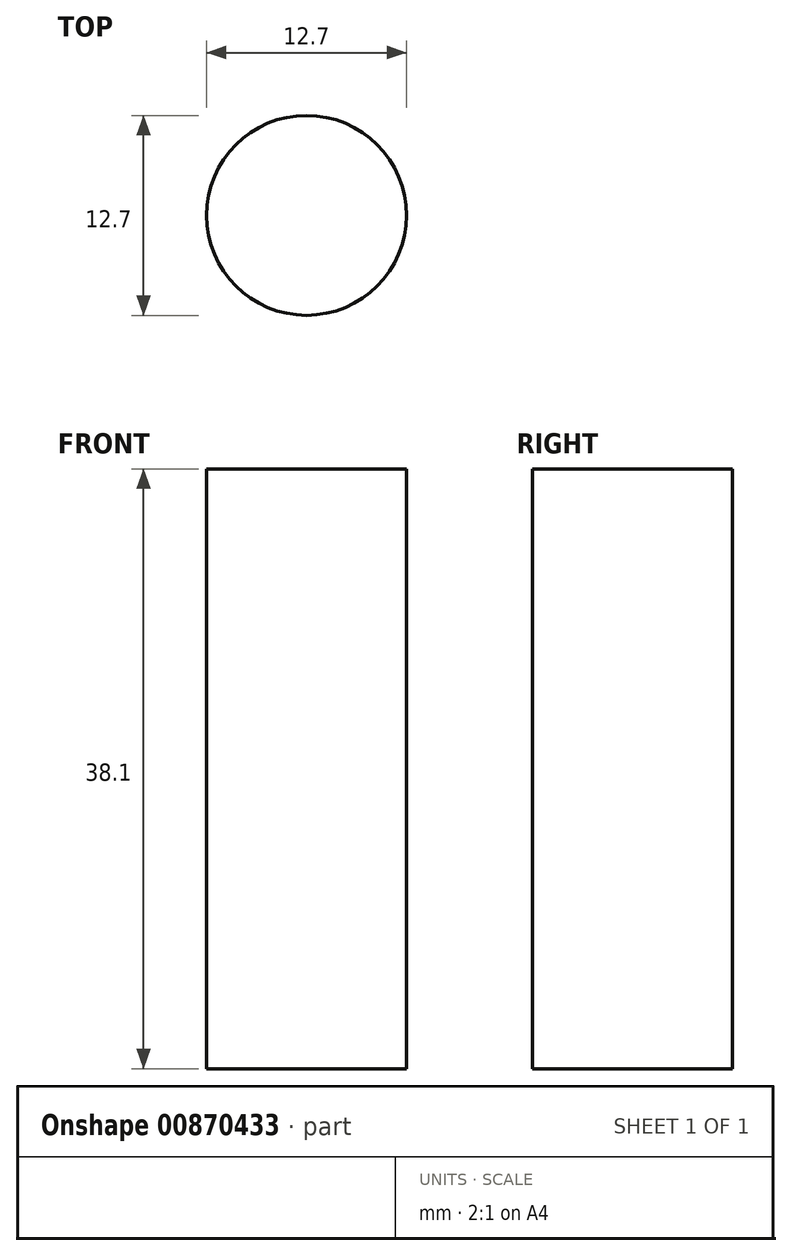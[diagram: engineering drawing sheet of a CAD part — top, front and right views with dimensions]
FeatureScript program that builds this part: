
annotation { "Feature Type Name" : "Feature", "Feature Type Description" : "" }
export const myFeature = defineFeature(function(context is Context, id is Id, definition is map)
    precondition{}
    {
        {
            var Q0;
            Q0=qCreatedBy(makeId("Top.planeOp"),FACE);
            var sketch = newSketch(context, id + "F0", { "sketchPlane" : qUnion([Q0])});
            skCircle(sketch, "E0", {"center": v(0, 0) * mm, "radius": 6.35 * mm});
            skSolve(sketch);
        }
        {
            var Q0;
            Q0=makeQuery(id+"F0.imprint","IMPRINT",FACE,{"disambiguationData":[TD([[makeQuery(id+"F0.imprint","IMPRINT",EDGE,{"derivedFrom":sQuery(id+"F0.wireOp",EDGE,"E0")}),1.0]])]});
            extrude(context, id + "F1", {"entities" : qUnion([Q0]), "depth" : 38.1 * mm, "offsetDistance" : 25.4 * mm});
        }
    });
